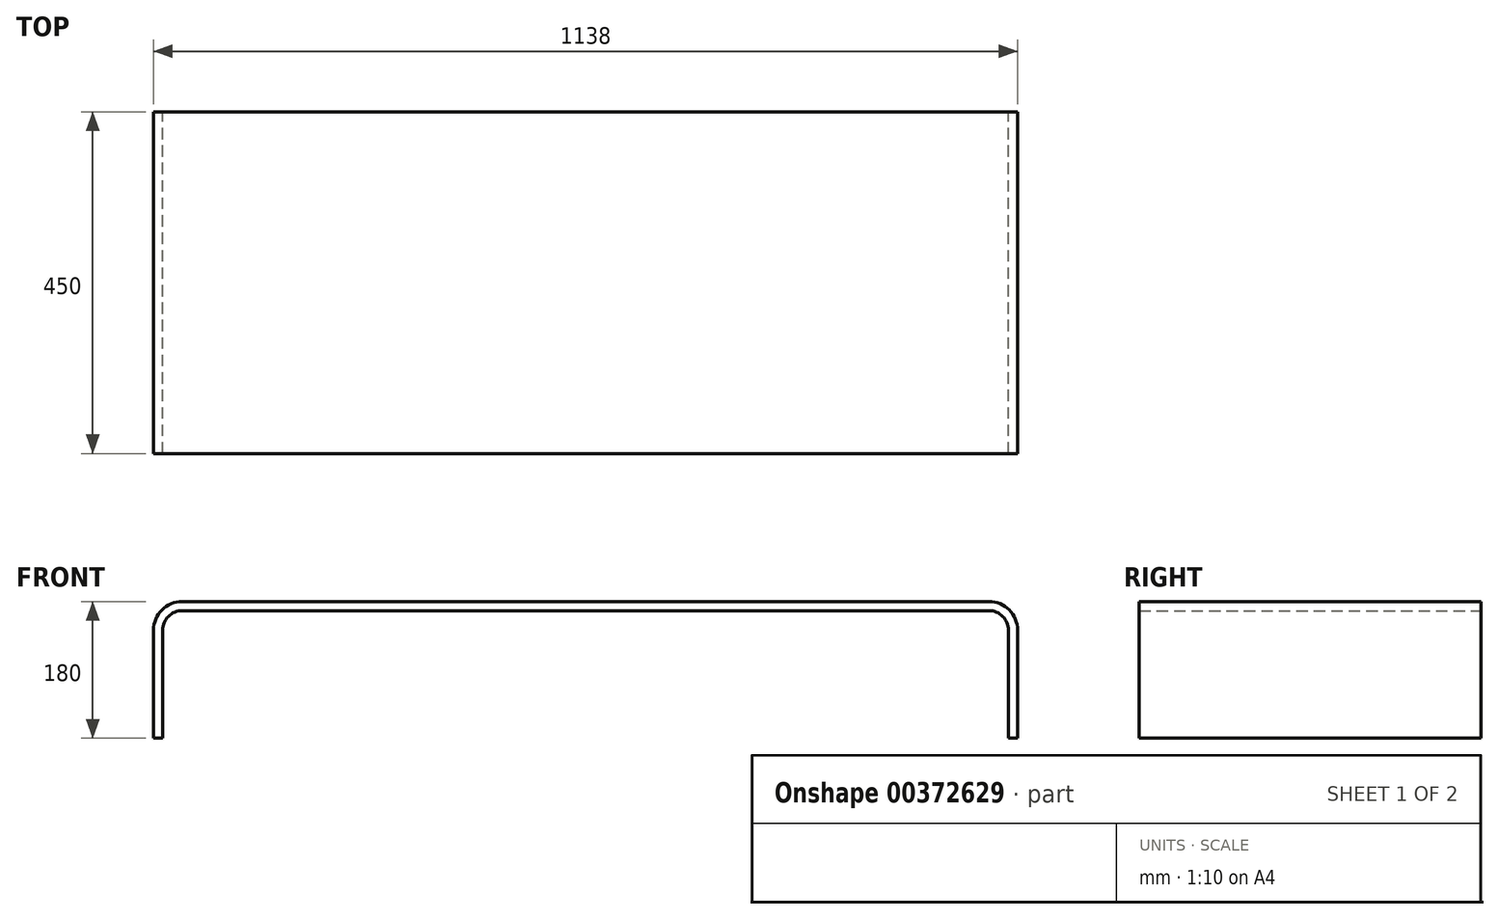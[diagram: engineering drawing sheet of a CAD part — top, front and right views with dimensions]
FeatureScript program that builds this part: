
annotation { "Feature Type Name" : "Feature", "Feature Type Description" : "" }
export const myFeature = defineFeature(function(context is Context, id is Id, definition is map)
    precondition{}
    {
        {
            var Q0;
            Q0=qCreatedBy(makeId("Front.planeOp"),FACE);
            var sketch = newSketch(context, id + "F0", { "sketchPlane" : qUnion([Q0])});
            skLineSegment(sketch, "E0", {"start": v(-531, 0) * mm, "end": v(531, 0) * mm});
            skLineSegment(sketch, "E1", {"start": v(569, -38) * mm, "end": v(569, -180) * mm});
            skLineSegment(sketch, "E2", {"start": v(-569, -180) * mm, "end": v(-569, -38) * mm});
            skPoint(sketch, "E3.visualSharp", {"position": v(-569, 0) * mm});
            skArc(sketch, "E3.filletArc", {"start": v(-531, 0) * mm, "mid": v(-557.87, -11.13) * mm, "end": v(-569, -38) * mm});
            skPoint(sketch, "E4.visualSharp", {"position": v(569, 0) * mm});
            skArc(sketch, "E4.filletArc", {"start": v(569, -38) * mm, "mid": v(557.87, -11.13) * mm, "end": v(531, 0) * mm});
            skLineSegment(sketch, "E5.0", {"start": v(557, -38) * mm, "end": v(557, -180) * mm});
            skLineSegment(sketch, "E5.1", {"start": v(-531, -12) * mm, "end": v(531, -12) * mm});
            skLineSegment(sketch, "E5.2", {"start": v(-557, -180) * mm, "end": v(-557, -38) * mm});
            skPoint(sketch, "E6.visualSharp", {"position": v(-557, -12) * mm});
            skPoint(sketch, "E7.visualSharp", {"position": v(557, -12) * mm});
            skArc(sketch, "E7.filletArc", {"start": v(557, -38) * mm, "mid": v(549.38, -19.62) * mm, "end": v(531, -12) * mm});
            skArc(sketch, "E8.filletArc", {"start": v(-531, -12) * mm, "mid": v(-549.38, -19.62) * mm, "end": v(-557, -38) * mm});
            skLineSegment(sketch, "E9", {"start": v(-569, -180) * mm, "end": v(-557, -180) * mm});
            skLineSegment(sketch, "E10", {"start": v(569, -180) * mm, "end": v(557, -180) * mm});
            skSolve(sketch);
        }
        {
            var Q0;
            Q0=qSketchRegion(id+"F0",true);
            extrude(context, id + "F1", {"entities" : qUnion([Q0]), "endBound" : BoundingType.SYMMETRIC, "depth" : 450 * mm});
        }
    });
